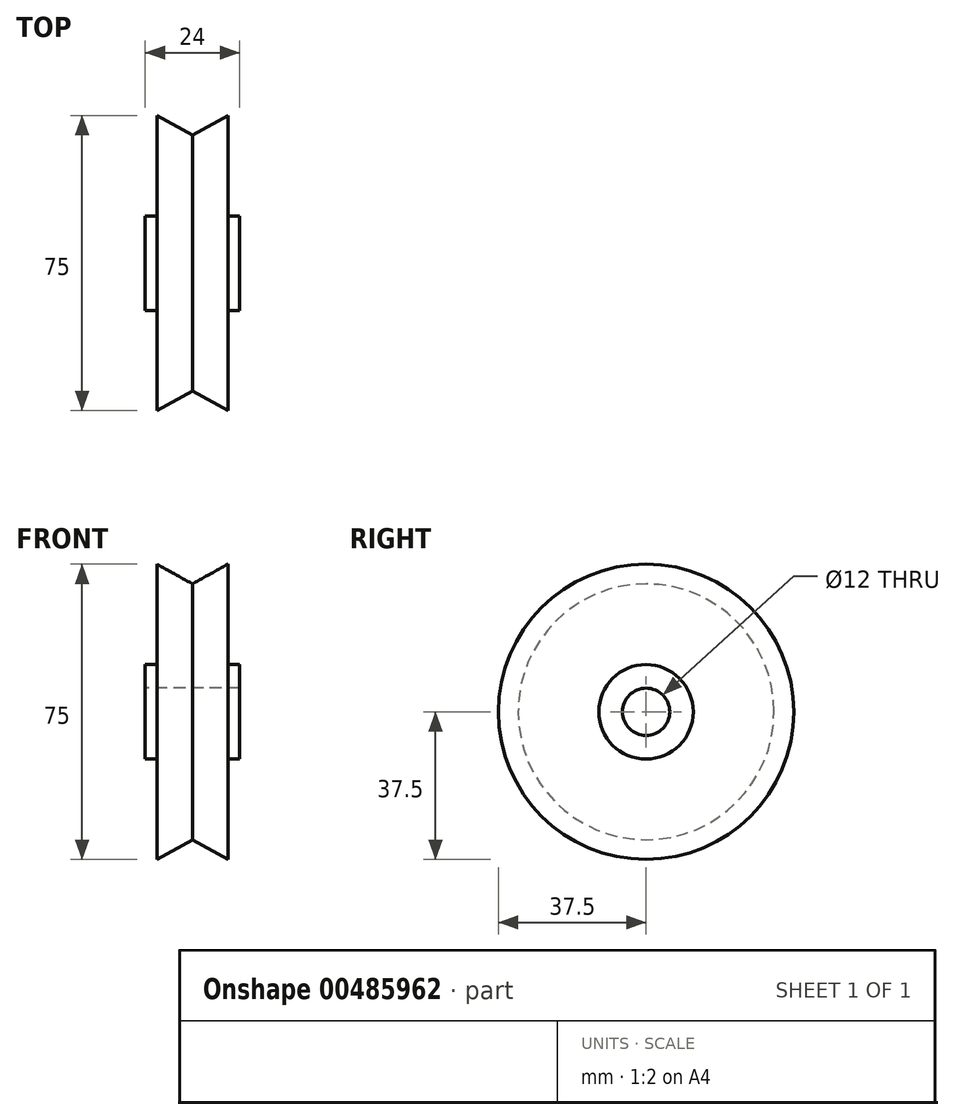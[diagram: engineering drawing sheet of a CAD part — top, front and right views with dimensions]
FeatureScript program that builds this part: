
annotation { "Feature Type Name" : "Feature", "Feature Type Description" : "" }
export const myFeature = defineFeature(function(context is Context, id is Id, definition is map)
    precondition{}
    {
        {
            var Q0;
            Q0=qCreatedBy(makeId("Top.planeOp"),FACE);
            var sketch = newSketch(context, id + "F0", { "sketchPlane" : qUnion([Q0])});
            skLineSegment(sketch, "E0", {"start": v(0, 47.97) * mm, "end": v(0, -45.27) * mm, "construction": true});
            skLineSegment(sketch, "E1", {"start": v(-40.81, 0) * mm, "end": v(48.24, 0) * mm, "construction": true});
            skLineSegment(sketch, "E2", {"start": v(-12, 6) * mm, "end": v(0, 6) * mm});
            skLineSegment(sketch, "E3", {"start": v(-12, 6) * mm, "end": v(-12, 12) * mm});
            skLineSegment(sketch, "E4", {"start": v(-12, 12) * mm, "end": v(-9, 12) * mm});
            skLineSegment(sketch, "E5", {"start": v(-9, 12) * mm, "end": v(-9, 37.5) * mm});
            skLineSegment(sketch, "E6", {"start": v(-9, 37.5) * mm, "end": v(0, 32.5) * mm});
            skLineSegment(sketch, "E7.MirrorCS", {"start": v(9, 37.5) * mm, "end": v(0, 32.5) * mm});
            skLineSegment(sketch, "E8.MirrorCS", {"start": v(9, 12) * mm, "end": v(9, 37.5) * mm});
            skLineSegment(sketch, "E9.MirrorCS", {"start": v(12, 6) * mm, "end": v(0, 6) * mm});
            skLineSegment(sketch, "E10.MirrorCS", {"start": v(12, 6) * mm, "end": v(12, 12) * mm});
            skLineSegment(sketch, "E11.MirrorCS", {"start": v(12, 12) * mm, "end": v(9, 12) * mm});
            skSolve(sketch);
        }
        {
            var Q0;
            Q0=makeQuery(id+"F0.imprint","IMPRINT",FACE,{"disambiguationData":[TD([[makeQuery(id+"F0.imprint","IMPRINT",EDGE,{"derivedFrom":sQuery(id+"F0.wireOp",EDGE,"E2")}),1.0]])]});
            var Q1;
            Q1=sQuery(id+"F0.wireOp",EDGE,"E1");
            revolve(context, id + "F1", {"entities" : qUnion([Q0]), "axis" : qUnion([Q1]), "revolveType" : RevolveType.FULL});
        }
    });
